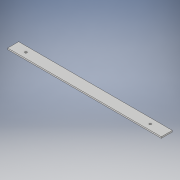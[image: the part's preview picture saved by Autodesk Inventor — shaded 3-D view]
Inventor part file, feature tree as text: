
AUTODESK INVENTOR PART (.ipt)
format: ipt  version: 2018.3 (Build 223284000, 284)  size: 105,472 bytes
history: native  units: in
note: dims shown in document units (in); Inventor stores cm internally (conversion verified against a paired STEP export)
features: extrude x2, sketch x2
ambient origin geometry x8: Origin, YZ Plane, XZ Plane, XY Plane, X Axis, Y Axis, Z Axis, Center Point
bodies: Solid1 (feature_tree)
feature tree (4):
  extrude  "Extrusion1"  Depth=1.0in
  extrude  "Extrusion2"  Depth=0.125in
  sketch  "Sketch1"  dims[d0=14.0in d1=1.0in]
  sketch  "Sketch2"  dims[d2=0.125in d3=0.0in d4=1.5in d5=11.335in d6=0.2031in d7=0.2031in d8=0.125in d9=0.0in]
